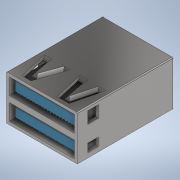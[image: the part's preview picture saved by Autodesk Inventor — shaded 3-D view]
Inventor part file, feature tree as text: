
AUTODESK INVENTOR PART (.ipt)
format: ipt  version: 2020 (Build 240168000, 168)  size: 651,264 bytes
history: native  units: in
note: dims shown in document units (in); Inventor stores cm internally (conversion verified against a paired STEP export)
features: extrude x10, chamfer x6, sketch x5, fillet x3
ambient origin geometry x8: Origin, YZ Plane, XZ Plane, XY Plane, X Axis, Y Axis, Z Axis, Center Point
bodies: Solid1 (feature_tree)
feature tree (24):
  extrude  "Extrusion1"  Depth=0.9408in
  sketch  "Sketch2"  dims[d3=0.5906in d4=0.0in d9=0.2165in]
  extrude  "Extrusion2"  Depth=0.2165in
  extrude  "Extrusion3"  Depth=0.0394in
  extrude  "Extrusion4"  Depth=0.0394in
  extrude  "Extrusion5"  Depth=0.0394in
  extrude  "Extrusion6"  Depth=0.0394in
  extrude  "Extrusion7"  Depth=0.0394in
  extrude  "Extrusion8"  Depth=0.0203in
  extrude  "Extrusion9"  Depth=0.0354in
  extrude  "Extrusion10"  Depth=1.1811in TaperAngle=0.0deg
  chamfer  "Chamfer1"  Distance=1.1811in
  chamfer  "Chamfer2"  Distance=0.1181in
  chamfer  "Chamfer3"  Distance=0.0394in
  chamfer  "Chamfer4"  Distance=0.0472in
  chamfer  "Chamfer5"  Distance=0.0472in
  chamfer  "Chamfer6"  Distance=0.0472in
  fillet  "Fillet1"  Radius=0.0472in
  fillet  "Fillet2"  Radius=0.0472in
  fillet  "Fillet3"  Radius=0.0354in
  sketch  "Sketch1"  dims[d1=1.2756in d2=0.9408in]
  sketch  "Sketch3"  dims[d10=0.2165in d11=0.0394in]
  sketch  "Sketch4"  dims[d13=0.0394in d14=0.0394in]
  sketch  "Sketch5"  dims[d15=0.0394in d17=0.0394in d18=0.0394in d19=7.874in d21=0.0394in d22=0.3937in d24=0.3937in d26=0.0203in d27=8.6614in d29=0.0354in d30=0.3937in d32=0.3937in d34=1.1811in d35=0.0in d36=1.1811in d37=0.0in d38=0.1181in d39=0.0in d40=0.0394in d41=0.0in d42=0.0472in d43=0.0in d44=0.0472in d45=0.0in d46=0.0472in d47=0.0in d48=0.0472in d49=0.0in d50=0.0472in d51=0.0in d52=0.0354in d53=0.0787in d54=45.0deg d55=0.0354in d56=0.0787in d57=45.0deg d58=0.0079in d59=0.0787in d60=45.0deg d61=0.0079in d62=0.0787in d63=45.0deg d64=0.0315in d65=0.0787in d66=45.0deg d67=0.0315in d68=0.0787in d69=45.0deg d70=0.0118in d71=0.0118in d72=0.0118in]
